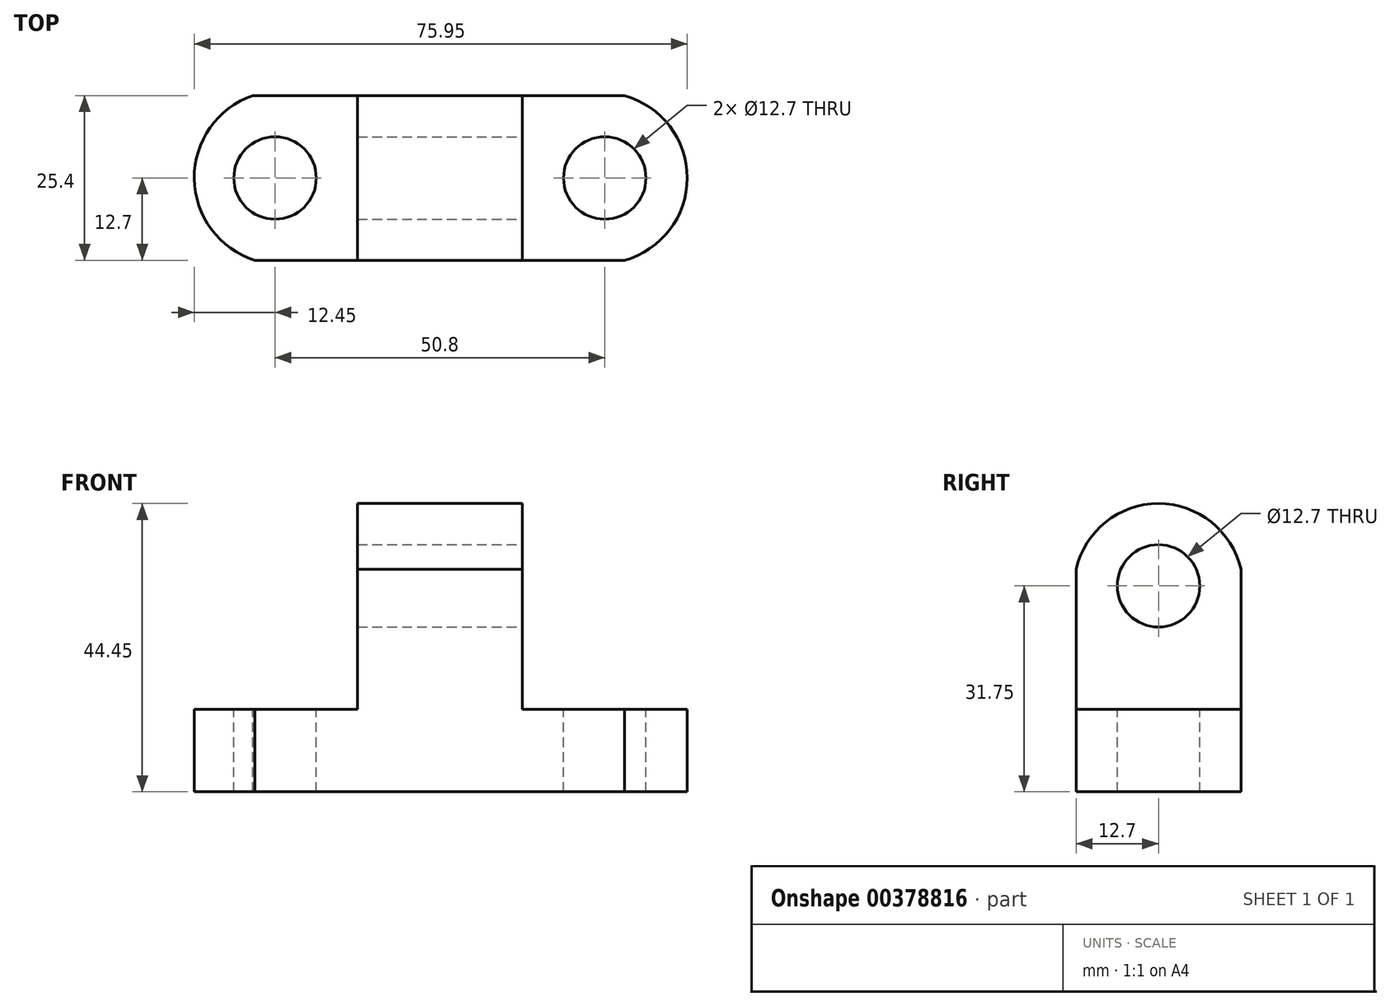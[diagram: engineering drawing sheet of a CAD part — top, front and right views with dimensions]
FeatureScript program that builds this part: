
annotation { "Feature Type Name" : "Feature", "Feature Type Description" : "" }
export const myFeature = defineFeature(function(context is Context, id is Id, definition is map)
    precondition{}
    {
        {
            var Q0;
            Q0=qCreatedBy(makeId("Front.planeOp"),FACE);
            var sketch = newSketch(context, id + "F0", { "sketchPlane" : qUnion([Q0])});
            skLineSegment(sketch, "E0", {"start": v(0, 0) * mm, "end": v(76.2, 0) * mm});
            skLineSegment(sketch, "E1", {"start": v(76.2, 0) * mm, "end": v(76.2, 12.7) * mm});
            skLineSegment(sketch, "E2", {"start": v(76.2, 12.7) * mm, "end": v(50.8, 12.7) * mm});
            skLineSegment(sketch, "E3", {"start": v(50.8, 12.7) * mm, "end": v(50.8, 44.45) * mm});
            skLineSegment(sketch, "E4", {"start": v(50.8, 44.45) * mm, "end": v(25.4, 44.45) * mm});
            skLineSegment(sketch, "E5", {"start": v(25.4, 44.45) * mm, "end": v(25.4, 12.7) * mm});
            skLineSegment(sketch, "E6", {"start": v(25.4, 12.7) * mm, "end": v(0, 12.7) * mm});
            skLineSegment(sketch, "E7", {"start": v(0, 12.7) * mm, "end": v(0, 0) * mm});
            skSolve(sketch);
        }
        {
            var Q0;
            Q0=makeQuery(id+"F0.imprint","IMPRINT",FACE,{"disambiguationData":[TD([[makeQuery(id+"F0.imprint","IMPRINT",EDGE,{"derivedFrom":sQuery(id+"F0.wireOp",EDGE,"E0")}),1.0]])]});
            extrude(context, id + "F1", {"entities" : qUnion([Q0]), "depth" : 25.4 * mm});
        }
        {
            var Q0;
            Q0=makeQuery(id+"F1.opExtrude","SWEPT_FACE",FACE,{"disambiguationData":[OSD([sQuery(id+"F0.wireOp",EDGE,"E3")])]});
            var sketch = newSketch(context, id + "F2", { "sketchPlane" : qUnion([Q0])});
            skCircle(sketch, "E8", {"center": v(-12.7, 31.75) * mm, "radius": 6.35 * mm});
            skSolve(sketch);
        }
        {
            var Q0;
            Q0=makeQuery(id+"F2.imprint","IMPRINT",FACE,{"disambiguationData":[TD([[makeQuery(id+"F2.imprint","IMPRINT",EDGE,{"derivedFrom":sQuery(id+"F2.wireOp",EDGE,"E8")}),1.0]])]});
            extrude(context, id + "F3", {"entities" : qUnion([Q0]), "operationType" : NewBodyOperationType.REMOVE, "oppositeDirection" : true, "depth" : 25.4 * mm});
        }
        {
            var Q0;
            Q0=makeQuery(id+"F1.opExtrude","SWEPT_FACE",FACE,{"disambiguationData":[OSD([sQuery(id+"F0.wireOp",EDGE,"E3")])]});
            var sketch = newSketch(context, id + "F4", { "sketchPlane" : qUnion([Q0])});
            skArc(sketch, "E9", {"start": v(0, 28.57) * mm, "mid": v(-12.7, 44.45) * mm, "end": v(-25.4, 28.57) * mm});
            skSolve(sketch);
        }
        {
            var Q0;
            Q0 = qSketchRegion(id + "F4", true);
            var Q1;
            {var subQ0=sQuery(id+"F4.wireOp",EDGE,"E9");var subQ1=sQuery(id+"F0.wireOp",EDGE,"E3");var subQ4=makeQuery(id+"F1.opExtrude","CAP_EDGE",EDGE,{"disambiguationData":[OSD([subQ1])],"isStart":false});var subQ5=makeQuery(id+"F4.imprint","INTERSECT",VERTEX,{"disambiguationData":[OD(1.0)],"derivedFrom":[subQ4,subQ0]});Q1=makeQuery(id+"F4.imprint","IMPRINT",FACE,{"disambiguationData":[TD([[makeQuery(id+"F4.imprint","IMPRINT",EDGE,{"disambiguationData":[TD([[subQ5,1.0]])],"derivedFrom":subQ0}),-1.0]])]});}
            var Q2;
            {var subQ0=sQuery(id+"F4.wireOp",EDGE,"E9");var subQ1=sQuery(id+"F0.wireOp",EDGE,"E3");var subQ2=makeQuery(id+"F1.opExtrude","CAP_EDGE",EDGE,{"disambiguationData":[OSD([subQ1])],"isStart":true});var subQ3=makeQuery(id+"F4.imprint","INTERSECT",VERTEX,{"disambiguationData":[OD(1.0)],"derivedFrom":[subQ2,subQ0]});Q2=makeQuery(id+"F4.imprint","IMPRINT",FACE,{"disambiguationData":[TD([[makeQuery(id+"F4.imprint","IMPRINT",EDGE,{"disambiguationData":[TD([[subQ3,-1.0]])],"derivedFrom":subQ0}),-1.0]])]});}
            extrude(context, id + "F5", {"entities" : qUnion([Q0, Q1, Q2]), "operationType" : NewBodyOperationType.REMOVE, "oppositeDirection" : true, "depth" : 25.4 * mm});
        }
        {
            var Q0;
            Q0=makeQuery(id+"F1.opExtrude","SWEPT_FACE",FACE,{"disambiguationData":[OSD([sQuery(id+"F0.wireOp",EDGE,"E2")])]});
            var sketch = newSketch(context, id + "F6", { "sketchPlane" : qUnion([Q0])});
            skCircle(sketch, "E10", {"center": v(63.5, -12.7) * mm, "radius": 6.35 * mm});
            skPoint(sketch, "E10.centerSnap0", {"position": v(63.5, -25.4) * mm});
            skSolve(sketch);
        }
        {
            var Q0;
            Q0=makeQuery(id+"F6.imprint","IMPRINT",FACE,{"disambiguationData":[TD([[makeQuery(id+"F6.imprint","IMPRINT",EDGE,{"derivedFrom":sQuery(id+"F6.wireOp",EDGE,"E10")}),1.0]])]});
            extrude(context, id + "F7", {"entities" : qUnion([Q0]), "operationType" : NewBodyOperationType.REMOVE, "oppositeDirection" : true, "depth" : 25.4 * mm});
        }
        {
            var Q0;
            Q0=makeQuery(id+"F1.opExtrude","SWEPT_FACE",FACE,{"disambiguationData":[OSD([sQuery(id+"F0.wireOp",EDGE,"E6")])]});
            var sketch = newSketch(context, id + "F8", { "sketchPlane" : qUnion([Q0])});
            skCircle(sketch, "E11", {"center": v(12.7, -12.7) * mm, "radius": 6.35 * mm});
            skPoint(sketch, "E11.centerSnap0", {"position": v(12.7, 0) * mm});
            skPoint(sketch, "E11.centerSnap1", {"position": v(25.4, -12.7) * mm});
            skSolve(sketch);
        }
        {
            var Q0;
            Q0=makeQuery(id+"F8.imprint","IMPRINT",FACE,{"disambiguationData":[TD([[makeQuery(id+"F8.imprint","IMPRINT",EDGE,{"derivedFrom":sQuery(id+"F8.wireOp",EDGE,"E11")}),1.0]])]});
            extrude(context, id + "F9", {"entities" : qUnion([Q0]), "operationType" : NewBodyOperationType.REMOVE, "oppositeDirection" : true, "depth" : 25.4 * mm});
        }
        {
            var Q0;
            Q0=makeQuery(id+"F1.opExtrude","SWEPT_FACE",FACE,{"disambiguationData":[OSD([sQuery(id+"F0.wireOp",EDGE,"E2")])]});
            var sketch = newSketch(context, id + "F10", { "sketchPlane" : qUnion([Q0])});
            skArc(sketch, "E12", {"start": v(59.52, -25.4) * mm, "mid": v(76.2, -12.7) * mm, "end": v(59.52, 0) * mm});
            skSolve(sketch);
        }
        {
            var Q0;
            Q0 = qSketchRegion(id + "F10", true);
            var Q1;
            {var subQ0=sQuery(id+"F10.wireOp",EDGE,"E12");var subQ1=sQuery(id+"F0.wireOp",EDGE,"E2");var subQ4=makeQuery(id+"F1.opExtrude","CAP_EDGE",EDGE,{"disambiguationData":[OSD([subQ1])],"isStart":true});var subQ5=makeQuery(id+"F10.imprint","INTERSECT",VERTEX,{"disambiguationData":[OD(1.0)],"derivedFrom":[subQ4,subQ0]});Q1=makeQuery(id+"F10.imprint","IMPRINT",FACE,{"disambiguationData":[TD([[makeQuery(id+"F10.imprint","IMPRINT",EDGE,{"disambiguationData":[TD([[subQ5,1.0]])],"derivedFrom":subQ0}),-1.0]])]});}
            var Q2;
            {var subQ0=sQuery(id+"F10.wireOp",EDGE,"E12");var subQ1=sQuery(id+"F0.wireOp",EDGE,"E2");var subQ2=makeQuery(id+"F1.opExtrude","CAP_EDGE",EDGE,{"disambiguationData":[OSD([subQ1])],"isStart":false});var subQ3=makeQuery(id+"F10.imprint","INTERSECT",VERTEX,{"disambiguationData":[OD(1.0)],"derivedFrom":[subQ2,subQ0]});Q2=makeQuery(id+"F10.imprint","IMPRINT",FACE,{"disambiguationData":[TD([[makeQuery(id+"F10.imprint","IMPRINT",EDGE,{"disambiguationData":[TD([[subQ3,-1.0]])],"derivedFrom":subQ0}),-1.0]])]});}
            extrude(context, id + "F11", {"entities" : qUnion([Q0, Q1, Q2]), "operationType" : NewBodyOperationType.REMOVE, "oppositeDirection" : true, "depth" : 25.4 * mm});
        }
        {
            var Q0;
            Q0=makeQuery(id+"F1.opExtrude","SWEPT_FACE",FACE,{"disambiguationData":[OSD([sQuery(id+"F0.wireOp",EDGE,"E6")])]});
            var sketch = newSketch(context, id + "F12", { "sketchPlane" : qUnion([Q0])});
            skArc(sketch, "E13", {"start": v(9.24, 0) * mm, "mid": v(0.25, -12.83) * mm, "end": v(9.6, -25.4) * mm});
            skSolve(sketch);
        }
        {
            var Q0;
            {var subQ0=sQuery(id+"F12.wireOp",EDGE,"E13");Q0=makeQuery(id+"F12.imprint","IMPRINT",FACE,{"disambiguationData":[TD([[makeQuery(id+"F12.imprint","IMPRINT",EDGE,{"derivedFrom":subQ0}),-1.0]])]});}
            extrude(context, id + "F13", {"entities" : qUnion([Q0]), "operationType" : NewBodyOperationType.REMOVE, "oppositeDirection" : true, "depth" : 25.4 * mm});
        }
    });
